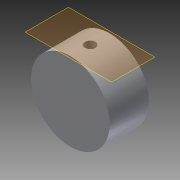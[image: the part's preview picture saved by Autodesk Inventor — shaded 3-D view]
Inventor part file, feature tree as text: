
AUTODESK INVENTOR PART (.ipt)
format: ipt  version: 2014 SP1 (Build 180222100, 222)  size: 88,576 bytes
history: native  units: in
note: dims shown in document units (in); Inventor stores cm internally (conversion verified against a paired STEP export)
features: extrude x2, sketch x2, plane x1
ambient origin geometry x8: Origin, YZ Plane, XZ Plane, XY Plane, X Axis, Y Axis, Z Axis, Center Point
bodies: Solid1 (feature_tree)
feature tree (5):
  extrude  "Extrusion1"  Depth=1.0in TaperAngle=0.0deg
  plane  "Work Plane1"
  extrude  "Extrusion2"  Depth=0.266in
  sketch  "Sketch1"  dims[d0=2.0in d1=1.0in d2=0.0in]
  sketch  "Sketch2"  dims[d3=0.5in d4=0.266in d5=2.0in d6=0.0in]
